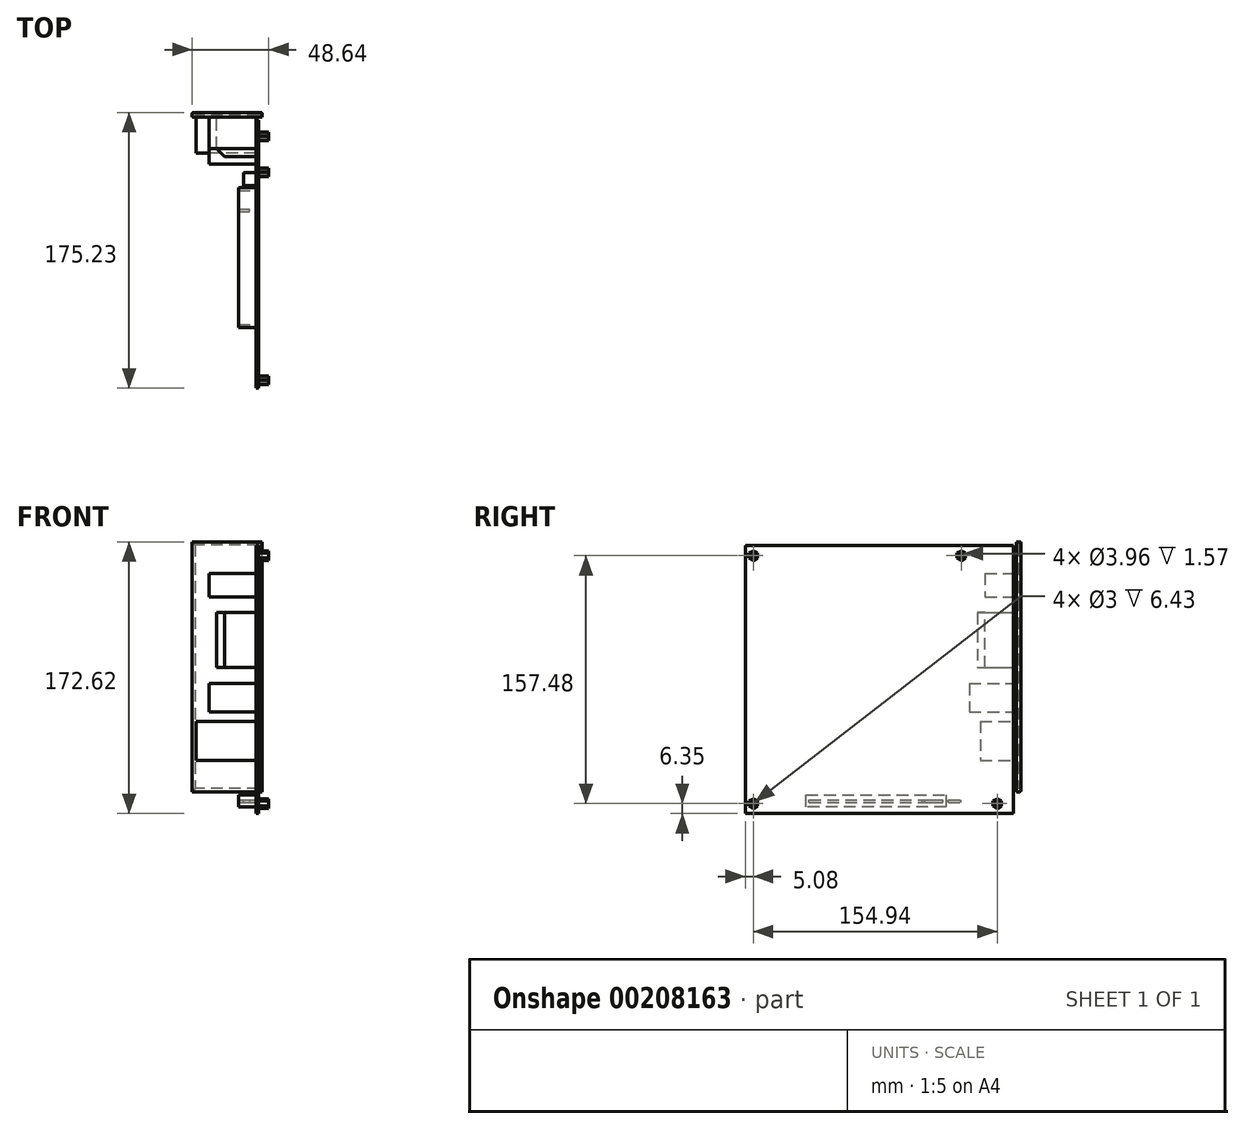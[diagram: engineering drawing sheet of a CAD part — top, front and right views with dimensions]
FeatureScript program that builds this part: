
annotation { "Feature Type Name" : "Feature", "Feature Type Description" : "" }
export const myFeature = defineFeature(function(context is Context, id is Id, definition is map)
    precondition{}
    {
        {
            var Q0;
            Q0=qCreatedBy(makeId("Right.planeOp"),FACE);
            var sketch = newSketch(context, id + "F0", { "sketchPlane" : qUnion([Q0])});
            skLineSegment(sketch, "E0.bottom", {"start": v(10.16, 209.55) * mm, "end": v(-160.02, 209.55) * mm});
            skLineSegment(sketch, "E0.top", {"start": v(10.16, 39.37) * mm, "end": v(-160.02, 39.37) * mm});
            skLineSegment(sketch, "E0.left", {"start": v(10.16, 209.55) * mm, "end": v(10.16, 39.37) * mm});
            skLineSegment(sketch, "E0.right", {"start": v(-160.02, 209.55) * mm, "end": v(-160.02, 39.37) * mm});
            skCircle(sketch, "E1", {"center": v(0, 45.72) * mm, "radius": 1.98 * mm});
            skCircle(sketch, "E2", {"center": v(-22.86, 203.2) * mm, "radius": 1.98 * mm});
            skCircle(sketch, "E3", {"center": v(-154.94, 45.72) * mm, "radius": 1.98 * mm});
            skCircle(sketch, "E4", {"center": v(-154.94, 203.2) * mm, "radius": 1.98 * mm});
            skLineSegment(sketch, "E5", {"start": v(10.16, 45.72) * mm, "end": v(0, 45.72) * mm});
            skLineSegment(sketch, "E6", {"start": v(10.16, 203.2) * mm, "end": v(-160.02, 203.2) * mm});
            skLineSegment(sketch, "E7", {"start": v(0, 209.55) * mm, "end": v(0, 39.37) * mm});
            skLineSegment(sketch, "E8", {"start": v(-154.94, 209.55) * mm, "end": v(-154.94, 203.2) * mm});
            skLineSegment(sketch, "E9", {"start": v(-22.86, 209.55) * mm, "end": v(-22.86, 203.2) * mm});
            skLineSegment(sketch, "E10", {"start": v(10.16, 0) * mm, "end": v(-160.02, 0) * mm});
            skCircle(sketch, "E11", {"center": v(0, 0) * mm, "radius": 1.98 * mm});
            skPoint(sketch, "E12", {"position": v(-46.94, 47.3) * mm});
            skLineSegment(sketch, "E13", {"start": v(-46.94, 51.04) * mm, "end": v(-32.44, 51.04) * mm});
            skLineSegment(sketch, "E14", {"start": v(-32.44, 51.04) * mm, "end": v(-32.44, 43.54) * mm});
            skLineSegment(sketch, "E15", {"start": v(-32.44, 43.54) * mm, "end": v(-46.94, 43.54) * mm});
            skLineSegment(sketch, "E16", {"start": v(-46.94, 43.54) * mm, "end": v(-121.44, 43.54) * mm});
            skLineSegment(sketch, "E17", {"start": v(-121.44, 43.54) * mm, "end": v(-121.44, 51.04) * mm});
            skLineSegment(sketch, "E18", {"start": v(-121.44, 51.04) * mm, "end": v(-46.94, 51.04) * mm});
            skLineSegment(sketch, "E19.bottom", {"start": v(-46.09, 48.1) * mm, "end": v(-34.44, 48.1) * mm});
            skLineSegment(sketch, "E19.top", {"start": v(-46.09, 46.49) * mm, "end": v(-34.44, 46.49) * mm});
            skLineSegment(sketch, "E19.left", {"start": v(-46.09, 46.49) * mm, "end": v(-46.09, 48.1) * mm});
            skLineSegment(sketch, "E19.right", {"start": v(-34.44, 46.49) * mm, "end": v(-34.44, 48.1) * mm});
            skLineSegment(sketch, "E20.bottom", {"start": v(-119.44, 48.1) * mm, "end": v(-47.79, 48.1) * mm});
            skLineSegment(sketch, "E20.top", {"start": v(-119.44, 46.5) * mm, "end": v(-47.79, 46.5) * mm});
            skLineSegment(sketch, "E20.left", {"start": v(-119.44, 46.5) * mm, "end": v(-119.44, 48.1) * mm});
            skLineSegment(sketch, "E20.right", {"start": v(-47.79, 46.5) * mm, "end": v(-47.79, 48.1) * mm});
            skPoint(sketch, "E21", {"position": v(-34.44, 47.29) * mm});
            skLineSegment(sketch, "E22.bottom", {"start": v(13.2, 53.24) * mm, "end": v(12.27, 53.24) * mm});
            skLineSegment(sketch, "E22.top", {"start": v(13.2, 212) * mm, "end": v(12.27, 212) * mm});
            skLineSegment(sketch, "E22.left", {"start": v(13.2, 53.24) * mm, "end": v(13.2, 212) * mm});
            skLineSegment(sketch, "E22.right", {"start": v(12.27, 53.24) * mm, "end": v(12.27, 212) * mm});
            skLineSegment(sketch, "E23.bottom", {"start": v(-31.14, 46.5) * mm, "end": v(-23.14, 46.5) * mm});
            skLineSegment(sketch, "E23.top", {"start": v(-31.14, 48.07) * mm, "end": v(-23.14, 48.07) * mm});
            skLineSegment(sketch, "E23.left", {"start": v(-31.14, 46.5) * mm, "end": v(-31.14, 48.08) * mm});
            skLineSegment(sketch, "E23.right", {"start": v(-23.14, 46.5) * mm, "end": v(-23.14, 48.07) * mm});
            skPoint(sketch, "E23.middle", {"position": v(-27.14, 47.3) * mm});
            skLineSegment(sketch, "E24", {"start": v(-34.8, 48.08) * mm, "end": v(-34.8, 46.5) * mm});
            skPoint(sketch, "E25", {"position": v(-34.8, 47.3) * mm});
            skSolve(sketch);
        }
        {
            var Q0;
            Q0=makeQuery(id+"F0.imprint","IMPRINT",FACE,{"disambiguationData":[TD([[makeQuery(id+"F0.imprint","IMPRINT",EDGE,{"derivedFrom":sQuery(id+"F0.wireOp",EDGE,"E0.bottom")}),1.0]])]});
            var Q1;
            Q1=makeQuery(id+"F0.imprint","IMPRINT",FACE,{"disambiguationData":[TD([[makeQuery(id+"F0.imprint","IMPRINT",EDGE,{"derivedFrom":sQuery(id+"F0.wireOp",EDGE,"E3")}),-1.0]])]});
            var Q2;
            {var subQ1=sQuery(id+"F0.wireOp",EDGE,"E0.left");var subQ7=sQuery(id+"F0.wireOp",EDGE,"E5");var subQ9=makeQuery(id+"F0.imprint","INTERSECT",VERTEX,{"derivedFrom":[subQ1,subQ7]});Q2=makeQuery(id+"F0.imprint","IMPRINT",FACE,{"disambiguationData":[TD([[makeQuery(id+"F0.imprint","IMPRINT",EDGE,{"disambiguationData":[TD([[subQ9,1.0]])],"derivedFrom":subQ1}),-1.0]])]});}
            var Q3;
            {var subQ7=sQuery(id+"F0.wireOp",EDGE,"E8");var subQ9=sQuery(id+"F0.wireOp",EDGE,"E0.bottom");var subQ10=makeQuery(id+"F0.imprint","INTERSECT",VERTEX,{"derivedFrom":[subQ9,subQ7]});Q3=makeQuery(id+"F0.imprint","IMPRINT",FACE,{"disambiguationData":[TD([[makeQuery(id+"F0.imprint","IMPRINT",EDGE,{"disambiguationData":[TD([[subQ10,1.0]])],"derivedFrom":subQ9}),1.0]])]});}
            var Q4;
            {var subQ0=sQuery(id+"F0.wireOp",EDGE,"E7");var subQ1=sQuery(id+"F0.wireOp",EDGE,"E0.bottom");var subQ2=makeQuery(id+"F0.imprint","INTERSECT",VERTEX,{"derivedFrom":[subQ1,subQ0]});Q4=makeQuery(id+"F0.imprint","IMPRINT",FACE,{"disambiguationData":[TD([[makeQuery(id+"F0.imprint","IMPRINT",EDGE,{"disambiguationData":[TD([[subQ2,-1.0]])],"derivedFrom":subQ1}),1.0]])]});}
            var Q5;
            {var subQ5=sQuery(id+"F0.wireOp",EDGE,"E0.left");var subQ6=sQuery(id+"F0.wireOp",EDGE,"E0.top");var subQ7=makeQuery(id+"F0.imprint","INTERSECT",VERTEX,{"derivedFrom":[subQ6,subQ5]});Q5=makeQuery(id+"F0.imprint","IMPRINT",FACE,{"disambiguationData":[TD([[makeQuery(id+"F0.imprint","IMPRINT",EDGE,{"disambiguationData":[TD([[subQ7,-1.0]])],"derivedFrom":subQ6}),-1.0]])]});}
            var Q6;
            Q6=makeQuery(id+"F0.imprint","IMPRINT",FACE,{"disambiguationData":[TD([[makeQuery(id+"F0.imprint","IMPRINT",EDGE,{"derivedFrom":sQuery(id+"F0.wireOp",EDGE,"E13")}),-1.0]])]});
            var Q7;
            Q7=makeQuery(id+"F0.imprint","IMPRINT",FACE,{"disambiguationData":[TD([[makeQuery(id+"F0.imprint","IMPRINT",EDGE,{"derivedFrom":sQuery(id+"F0.wireOp",EDGE,"E19.bottom")}),-1.0]])]});
            var Q8;
            Q8=makeQuery(id+"F0.imprint","IMPRINT",FACE,{"disambiguationData":[TD([[makeQuery(id+"F0.imprint","IMPRINT",EDGE,{"derivedFrom":sQuery(id+"F0.wireOp",EDGE,"E20.bottom")}),-1.0]])]});
            var Q9;
            {var subQ1=sQuery(id+"F0.wireOp",EDGE,"E0.right");var subQ5=sQuery(id+"F0.wireOp",EDGE,"E0.bottom");var subQ6=makeQuery(id+"F0.imprint","INTERSECT",VERTEX,{"derivedFrom":[subQ5,subQ1]});Q9=makeQuery(id+"F0.imprint","IMPRINT",FACE,{"disambiguationData":[TD([[makeQuery(id+"F0.imprint","IMPRINT",EDGE,{"disambiguationData":[TD([[subQ6,1.0]])],"derivedFrom":subQ5}),1.0]])]});}
            var Q10;
            Q10=makeQuery(id+"F0.imprint","IMPRINT",FACE,{"disambiguationData":[TD([[makeQuery(id+"F0.imprint","IMPRINT",EDGE,{"derivedFrom":sQuery(id+"F0.wireOp",EDGE,"E23.bottom")}),1.0]])]});
            extrude(context, id + "F1", {"entities" : qUnion([Q0, Q1, Q2, Q3, Q4, Q5, Q6, Q7, Q8, Q9, Q10]), "depth" : 1.57 * mm});
        }
        {
            var Q0;
            Q0=makeQuery(id+"F0.imprint","IMPRINT",FACE,{"disambiguationData":[TD([[makeQuery(id+"F0.imprint","IMPRINT",EDGE,{"derivedFrom":sQuery(id+"F0.wireOp",EDGE,"E13")}),-1.0]])]});
            extrude(context, id + "F2", {"entities" : qUnion([Q0]), "operationType" : NewBodyOperationType.ADD, "oppositeDirection" : true, "depth" : 11.25 * mm});
        }
        {
            var Q0;
            Q0=makeQuery(id+"F1.opExtrude","CAP_FACE",FACE,{"disambiguationData":[OSD([sQuery(id+"F0.wireOp",EDGE,"E0.bottom"),sQuery(id+"F0.wireOp",EDGE,"E0.top"),sQuery(id+"F0.wireOp",EDGE,"E0.left"),sQuery(id+"F0.wireOp",EDGE,"E0.right"),sQuery(id+"F0.wireOp",EDGE,"E1"),sQuery(id+"F0.wireOp",EDGE,"E2"),sQuery(id+"F0.wireOp",EDGE,"E3"),sQuery(id+"F0.wireOp",EDGE,"E4")])],"isStart":false});
            var sketch = newSketch(context, id + "F3", { "sketchPlane" : qUnion([Q0])});
            skCircle(sketch, "E26.cCircle", {"center": v(-154.94, 203.2) * mm, "radius": 3 * mm, "construction": true});
            skLineSegment(sketch, "E26.0", {"start": v(-152.34, 201.7) * mm, "end": v(-154.94, 200.2) * mm});
            skLineSegment(sketch, "E26.1", {"start": v(-154.94, 200.2) * mm, "end": v(-157.54, 201.7) * mm});
            skLineSegment(sketch, "E26.2", {"start": v(-157.54, 201.7) * mm, "end": v(-157.54, 204.7) * mm});
            skLineSegment(sketch, "E26.3", {"start": v(-157.54, 204.7) * mm, "end": v(-154.94, 206.2) * mm});
            skLineSegment(sketch, "E26.4", {"start": v(-154.94, 206.2) * mm, "end": v(-152.34, 204.7) * mm});
            skLineSegment(sketch, "E26.5", {"start": v(-152.34, 204.7) * mm, "end": v(-152.34, 201.7) * mm});
            skCircle(sketch, "E27", {"center": v(-154.94, 203.2) * mm, "radius": 1.5 * mm});
            skCircle(sketch, "E28", {"center": v(0, 45.72) * mm, "radius": 1.5 * mm});
            skCircle(sketch, "E29", {"center": v(-22.86, 203.2) * mm, "radius": 1.5 * mm});
            skCircle(sketch, "E30", {"center": v(-154.94, 45.72) * mm, "radius": 1.5 * mm});
            skCircle(sketch, "E31.cCircle", {"center": v(-154.94, 45.72) * mm, "radius": 3 * mm, "construction": true});
            skLineSegment(sketch, "E31.0", {"start": v(-152.34, 44.22) * mm, "end": v(-154.94, 42.72) * mm});
            skLineSegment(sketch, "E31.1", {"start": v(-154.94, 42.72) * mm, "end": v(-157.54, 44.22) * mm});
            skLineSegment(sketch, "E31.2", {"start": v(-157.54, 44.22) * mm, "end": v(-157.54, 47.22) * mm});
            skLineSegment(sketch, "E31.3", {"start": v(-157.54, 47.22) * mm, "end": v(-154.94, 48.72) * mm});
            skLineSegment(sketch, "E31.4", {"start": v(-154.94, 48.72) * mm, "end": v(-152.34, 47.22) * mm});
            skLineSegment(sketch, "E31.5", {"start": v(-152.34, 47.22) * mm, "end": v(-152.34, 44.22) * mm});
            skCircle(sketch, "E32.cCircle", {"center": v(0, 45.72) * mm, "radius": 3 * mm, "construction": true});
            skLineSegment(sketch, "E32.0", {"start": v(2.6, 44.22) * mm, "end": v(0, 42.72) * mm});
            skLineSegment(sketch, "E32.1", {"start": v(0, 42.72) * mm, "end": v(-2.6, 44.22) * mm});
            skLineSegment(sketch, "E32.2", {"start": v(-2.6, 44.22) * mm, "end": v(-2.6, 47.22) * mm});
            skLineSegment(sketch, "E32.3", {"start": v(-2.6, 47.22) * mm, "end": v(0, 48.72) * mm});
            skLineSegment(sketch, "E32.4", {"start": v(0, 48.72) * mm, "end": v(2.6, 47.22) * mm});
            skLineSegment(sketch, "E32.5", {"start": v(2.6, 47.22) * mm, "end": v(2.6, 44.22) * mm});
            skCircle(sketch, "E33.cCircle", {"center": v(-22.86, 203.2) * mm, "radius": 3 * mm, "construction": true});
            skLineSegment(sketch, "E33.0", {"start": v(-20.26, 201.7) * mm, "end": v(-22.86, 200.2) * mm});
            skLineSegment(sketch, "E33.1", {"start": v(-22.86, 200.2) * mm, "end": v(-25.46, 201.7) * mm});
            skLineSegment(sketch, "E33.2", {"start": v(-25.46, 201.7) * mm, "end": v(-25.46, 204.7) * mm});
            skLineSegment(sketch, "E33.3", {"start": v(-25.46, 204.7) * mm, "end": v(-22.86, 206.2) * mm});
            skLineSegment(sketch, "E33.4", {"start": v(-22.86, 206.2) * mm, "end": v(-20.26, 204.7) * mm});
            skLineSegment(sketch, "E33.5", {"start": v(-20.26, 204.7) * mm, "end": v(-20.26, 201.7) * mm});
            skSolve(sketch);
        }
        {
            var Q0;
            Q0 = qSketchRegion(id + "F3", true);
            extrude(context, id + "F4", {"entities" : qUnion([Q0]), "operationType" : NewBodyOperationType.ADD, "depth" : 6.43 * mm});
        }
        {
            var Q0;
            Q0=makeQuery(id+"F0.imprint","IMPRINT",FACE,{"disambiguationData":[TD([[makeQuery(id+"F0.imprint","IMPRINT",EDGE,{"derivedFrom":sQuery(id+"F0.wireOp",EDGE,"E22.bottom")}),-1.0]])]});
            extrude(context, id + "F5", {"entities" : qUnion([Q0]), "depth" : 3.81 * mm, "hasSecondDirection" : true, "secondDirectionOppositeDirection" : true, "secondDirectionDepth" : (44.45 - 3.81) * mm});
        }
        {
            var Q0;
            Q0=makeQuery(id+"F5.opExtrude","SWEPT_FACE",FACE,{"disambiguationData":[OSD([sQuery(id+"F0.wireOp",EDGE,"E22.left")])]});
            var sketch = newSketch(context, id + "F6", { "sketchPlane" : qUnion([Q0])});
            skLineSegment(sketch, "E34.bottom", {"start": v(-1.8, 210) * mm, "end": v(38.64, 210) * mm});
            skLineSegment(sketch, "E34.top", {"start": v(-1.8, 55.24) * mm, "end": v(38.64, 55.24) * mm});
            skLineSegment(sketch, "E34.left", {"start": v(-1.8, 210) * mm, "end": v(-1.8, 55.24) * mm});
            skLineSegment(sketch, "E34.right", {"start": v(38.64, 210) * mm, "end": v(38.64, 55.24) * mm});
            skLineSegment(sketch, "E35.bottom", {"start": v(-3.81, 212) * mm, "end": v(40.64, 212) * mm});
            skLineSegment(sketch, "E35.top", {"start": v(-3.8, 53.24) * mm, "end": v(40.64, 53.24) * mm});
            skLineSegment(sketch, "E35.left", {"start": v(-3.81, 212) * mm, "end": v(-3.81, 53.24) * mm});
            skLineSegment(sketch, "E35.right", {"start": v(40.64, 212) * mm, "end": v(40.64, 53.24) * mm});
            skSolve(sketch);
        }
        {
            var Q0;
            Q0=makeQuery(id+"F6.imprint","IMPRINT",FACE,{"disambiguationData":[TD([[makeQuery(id+"F6.imprint","IMPRINT",EDGE,{"derivedFrom":sQuery(id+"F6.wireOp",EDGE,"E34.bottom")}),1.0]])]});
            extrude(context, id + "F7", {"entities" : qUnion([Q0]), "operationType" : NewBodyOperationType.ADD, "depth" : 2 * mm});
        }
        {
            var Q0;
            Q0=makeQuery(id+"F7.opExtrude","CAP_EDGE",EDGE,{"disambiguationData":[OSD([sQuery(id+"F6.wireOp",EDGE,"E34.left")])],"isStart":false});
            var Q1;
            Q1=makeQuery(id+"F7.opExtrude","CAP_EDGE",EDGE,{"disambiguationData":[OSD([sQuery(id+"F6.wireOp",EDGE,"E34.bottom")])],"isStart":false});
            var Q2;
            Q2=makeQuery(id+"F7.opExtrude","CAP_EDGE",EDGE,{"disambiguationData":[OSD([sQuery(id+"F6.wireOp",EDGE,"E34.right")])],"isStart":false});
            var Q3;
            Q3=makeQuery(id+"F7.opExtrude","CAP_EDGE",EDGE,{"disambiguationData":[OSD([sQuery(id+"F6.wireOp",EDGE,"E34.top")])],"isStart":false});
            var Q4;
            Q4=makeQuery(id+"F7.opExtrude","CAP_EDGE",EDGE,{"disambiguationData":[OSD([sQuery(id+"F6.wireOp",EDGE,"E35.top")])],"isStart":false});
            var Q5;
            Q5=makeQuery(id+"F7.opExtrude","CAP_EDGE",EDGE,{"disambiguationData":[OSD([sQuery(id+"F6.wireOp",EDGE,"E35.right")])],"isStart":false});
            var Q6;
            Q6=makeQuery(id+"F7.opExtrude","CAP_EDGE",EDGE,{"disambiguationData":[OSD([sQuery(id+"F6.wireOp",EDGE,"E35.left")])],"isStart":false});
            var Q7;
            Q7=makeQuery(id+"F7.opExtrude","CAP_EDGE",EDGE,{"disambiguationData":[OSD([sQuery(id+"F6.wireOp",EDGE,"E35.bottom")])],"isStart":false});
            fillet(context, id + "F8", {"entities" : qUnion([Q0, Q1, Q2, Q3, Q4, Q5, Q6, Q7]), "radius" : 1 * mm, "tangentPropagation" : true, "allowEdgeOverflow" : false});
        }
        {
            var Q0;
            Q0=makeQuery(id+"F5.opExtrude","SWEPT_FACE",FACE,{"disambiguationData":[OSD([sQuery(id+"F0.wireOp",EDGE,"E22.right")])]});
            var sketch = newSketch(context, id + "F9", { "sketchPlane" : qUnion([Q0])});
            skLineSegment(sketch, "E36.bottom", {"start": v(-30, 192) * mm, "end": v(0, 192) * mm});
            skLineSegment(sketch, "E36.top", {"start": v(-30, 177) * mm, "end": v(0, 177) * mm});
            skLineSegment(sketch, "E36.left", {"start": v(-30, 192) * mm, "end": v(-30, 177) * mm});
            skLineSegment(sketch, "E36.right", {"start": v(0, 192) * mm, "end": v(0, 177) * mm});
            skLineSegment(sketch, "E37.bottom", {"start": v(-25, 167) * mm, "end": v(0, 167) * mm});
            skLineSegment(sketch, "E37.top", {"start": v(-25, 132) * mm, "end": v(0, 132) * mm});
            skLineSegment(sketch, "E37.left", {"start": v(-25, 167) * mm, "end": v(-25, 132) * mm});
            skLineSegment(sketch, "E37.right", {"start": v(0, 167) * mm, "end": v(0, 132) * mm});
            skLineSegment(sketch, "E38.bottom", {"start": v(0, 122) * mm, "end": v(-30, 122) * mm});
            skLineSegment(sketch, "E38.top", {"start": v(0, 104) * mm, "end": v(-30, 104) * mm});
            skLineSegment(sketch, "E38.left", {"start": v(0, 122) * mm, "end": v(0, 104) * mm});
            skLineSegment(sketch, "E38.right", {"start": v(-30, 122) * mm, "end": v(-30, 104) * mm});
            skLineSegment(sketch, "E39.bottom", {"start": v(0, 98) * mm, "end": v(-38, 98) * mm});
            skLineSegment(sketch, "E39.top", {"start": v(0, 73) * mm, "end": v(-38, 73) * mm});
            skLineSegment(sketch, "E39.left", {"start": v(0, 98) * mm, "end": v(0, 73) * mm});
            skLineSegment(sketch, "E39.right", {"start": v(-38, 98) * mm, "end": v(-38, 73) * mm});
            skSolve(sketch);
        }
        {
            var Q0;
            Q0=makeQuery(id+"F9.imprint","IMPRINT",FACE,{"disambiguationData":[TD([[makeQuery(id+"F9.imprint","IMPRINT",EDGE,{"derivedFrom":sQuery(id+"F9.wireOp",EDGE,"E36.bottom")}),-1.0]])]});
            extrude(context, id + "F10", {"entities" : qUnion([Q0]), "operationType" : NewBodyOperationType.ADD, "depth" : 20 * mm});
        }
        {
            var Q0;
            Q0=makeQuery(id+"F9.imprint","IMPRINT",FACE,{"disambiguationData":[TD([[makeQuery(id+"F9.imprint","IMPRINT",EDGE,{"derivedFrom":sQuery(id+"F9.wireOp",EDGE,"E37.bottom")}),-1.0]])]});
            extrude(context, id + "F11", {"entities" : qUnion([Q0]), "operationType" : NewBodyOperationType.ADD, "depth" : 25 * mm});
        }
        {
            var Q0;
            Q0=makeQuery(id+"F9.imprint","IMPRINT",FACE,{"disambiguationData":[TD([[makeQuery(id+"F9.imprint","IMPRINT",EDGE,{"derivedFrom":sQuery(id+"F9.wireOp",EDGE,"E38.bottom")}),1.0]])]});
            extrude(context, id + "F12", {"entities" : qUnion([Q0]), "operationType" : NewBodyOperationType.ADD, "depth" : 30 * mm});
        }
        {
            var Q0;
            Q0=makeQuery(id+"F9.imprint","IMPRINT",FACE,{"disambiguationData":[TD([[makeQuery(id+"F9.imprint","IMPRINT",EDGE,{"derivedFrom":sQuery(id+"F9.wireOp",EDGE,"E39.bottom")}),1.0]])]});
            extrude(context, id + "F13", {"entities" : qUnion([Q0]), "operationType" : NewBodyOperationType.ADD, "depth" : 23 * mm});
        }
        {
            var Q0;
            Q0=makeQuery(id+"F11.opExtrude","CAP_EDGE",EDGE,{"disambiguationData":[OSD([sQuery(id+"F9.wireOp",EDGE,"E37.left")])],"isStart":false});
            chamfer(context, id + "F14", {"entities" : qUnion([Q0]), "width" : 5 * mm, "tangentPropagation" : true});
        }
        {
            var Q0;
            Q0=makeQuery(id+"F2.opExtrude","SWEPT_FACE",FACE,{"disambiguationData":[OSD([sQuery(id+"F0.wireOp",EDGE,"E19.left")])]});
            var sketch = newSketch(context, id + "F15", { "sketchPlane" : qUnion([Q0])});
            skLineSegment(sketch, "E40.bottom", {"start": v(0, 46.49) * mm, "end": v(4, 46.49) * mm});
            skLineSegment(sketch, "E40.top", {"start": v(0, 48.1) * mm, "end": v(4, 48.1) * mm});
            skLineSegment(sketch, "E40.left", {"start": v(0, 46.49) * mm, "end": v(0, 48.1) * mm});
            skLineSegment(sketch, "E41", {"start": v(4, 48.1) * mm, "end": v(4, 46.49) * mm});
            skSolve(sketch);
        }
        {
            var Q0;
            Q0 = qSketchRegion(id + "F15", true);
            extrude(context, id + "F16", {"entities" : qUnion([Q0]), "operationType" : NewBodyOperationType.REMOVE, "oppositeDirection" : true, "depth" : 2 * mm});
        }
        {
            var Q0;
            Q0=makeQuery(id+"F0.imprint","IMPRINT",FACE,{"disambiguationData":[TD([[makeQuery(id+"F0.imprint","IMPRINT",EDGE,{"derivedFrom":sQuery(id+"F0.wireOp",EDGE,"E23.bottom")}),1.0]])]});
            extrude(context, id + "F17", {"entities" : qUnion([Q0]), "operationType" : NewBodyOperationType.ADD, "oppositeDirection" : true, "depth" : 7.9 * mm});
        }
    });
